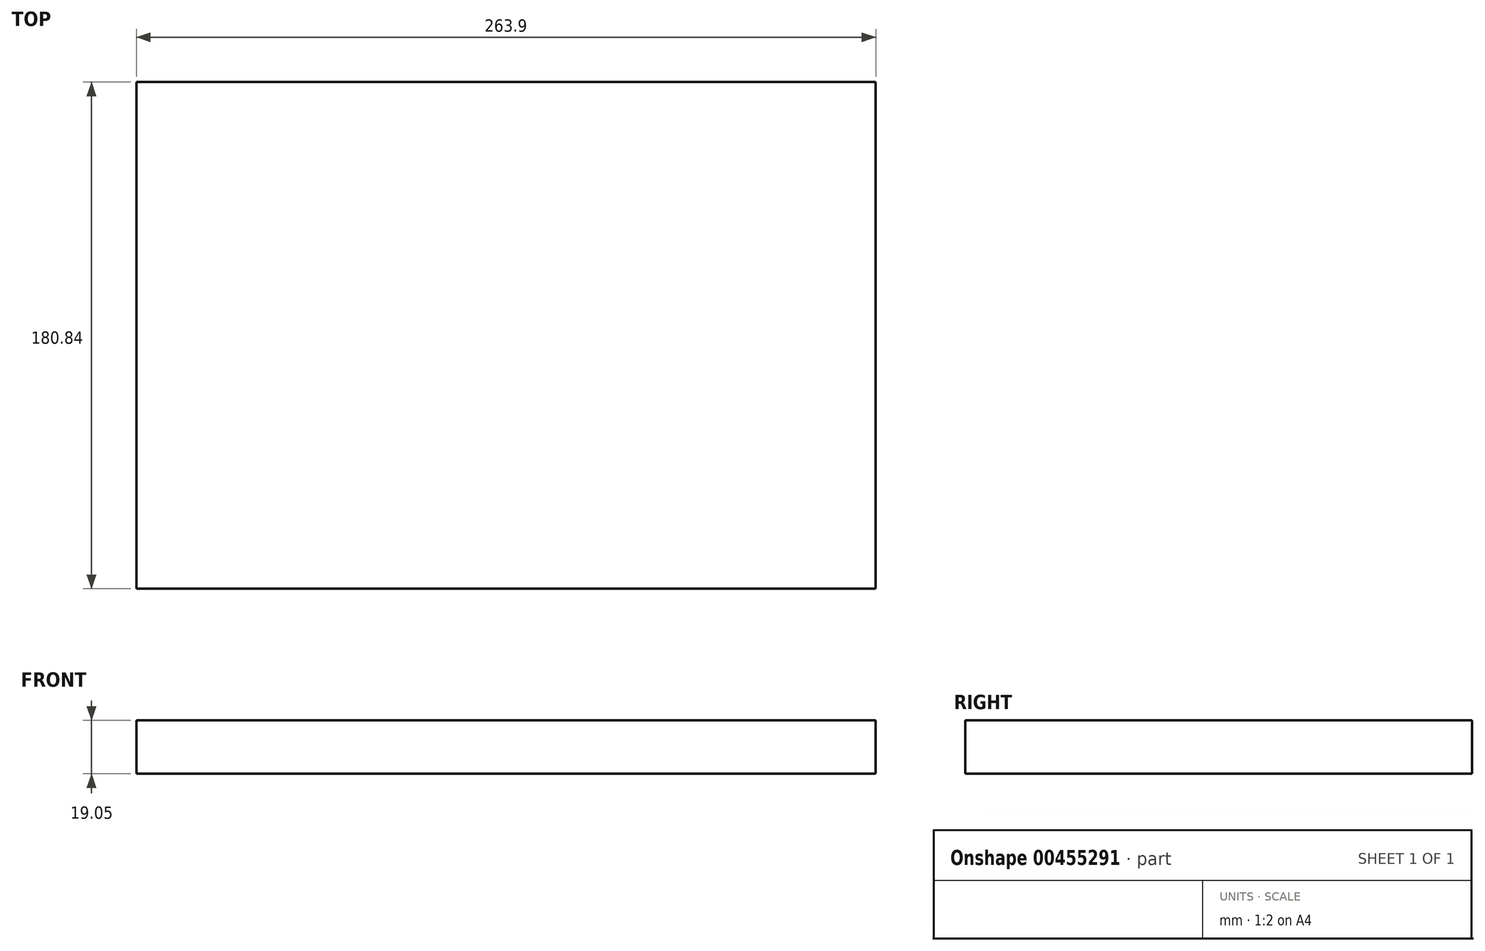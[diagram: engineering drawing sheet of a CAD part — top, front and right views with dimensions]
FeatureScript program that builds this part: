
annotation { "Feature Type Name" : "Feature", "Feature Type Description" : "" }
export const myFeature = defineFeature(function(context is Context, id is Id, definition is map)
    precondition{}
    {
        {
            var Q0;
            Q0=qCreatedBy(makeId("Top.planeOp"),FACE);
            var sketch = newSketch(context, id + "F0", { "sketchPlane" : qUnion([Q0])});
            skLineSegment(sketch, "E0.bottom", {"start": v(-119.1, 49.23) * mm, "end": v(144.8, 49.23) * mm});
            skLineSegment(sketch, "E0.top", {"start": v(-119.1, -131.6) * mm, "end": v(144.8, -131.6) * mm});
            skLineSegment(sketch, "E0.left", {"start": v(-119.1, 49.23) * mm, "end": v(-119.1, -131.6) * mm});
            skLineSegment(sketch, "E0.right", {"start": v(144.8, 49.23) * mm, "end": v(144.8, -131.6) * mm});
            skSolve(sketch);
        }
        {
            var Q0;
            Q0=makeQuery(id+"F0.imprint","IMPRINT",FACE,{"disambiguationData":[TD([[makeQuery(id+"F0.imprint","IMPRINT",EDGE,{"derivedFrom":sQuery(id+"F0.wireOp",EDGE,"E0.bottom")}),-1.0]])]});
            extrude(context, id + "F1", {"entities" : qUnion([Q0]), "depth" : 19.05 * mm});
        }
    });
